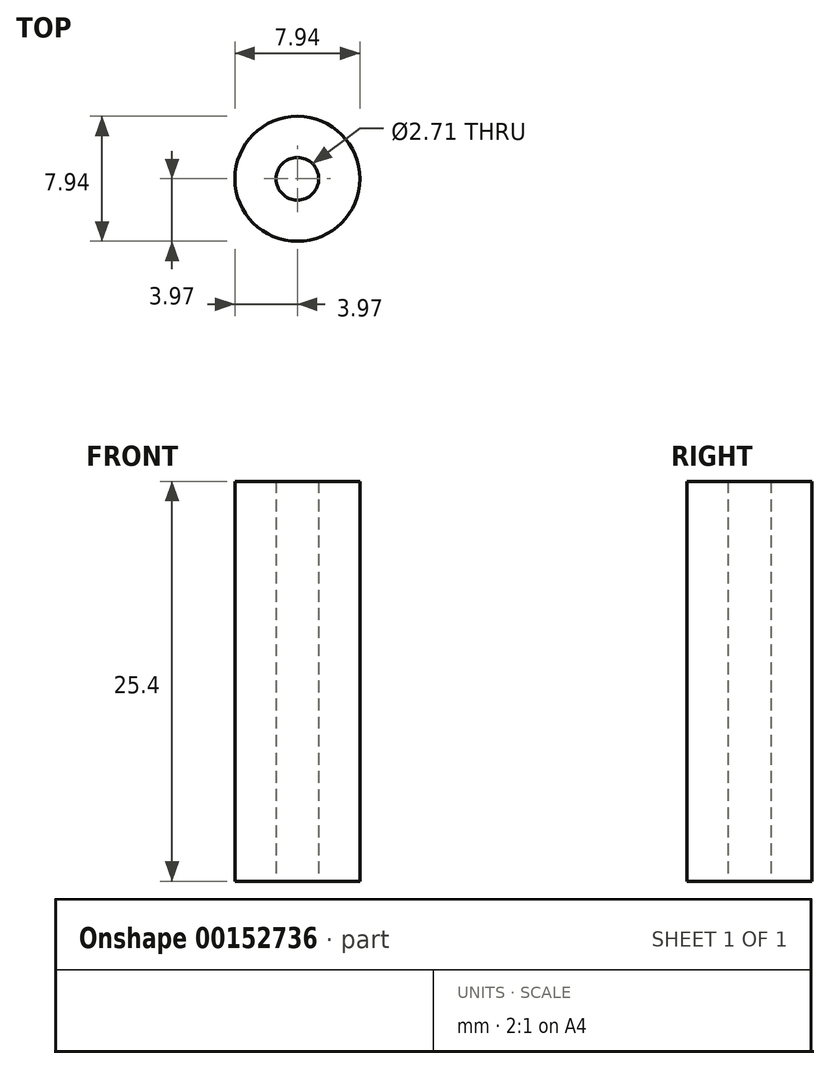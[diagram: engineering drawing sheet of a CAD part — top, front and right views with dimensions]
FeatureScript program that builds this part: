
annotation { "Feature Type Name" : "Feature", "Feature Type Description" : "" }
export const myFeature = defineFeature(function(context is Context, id is Id, definition is map)
    precondition{}
    {
        {
            var Q0;
            Q0=qCreatedBy(makeId("Top.planeOp"),FACE);
            var sketch = newSketch(context, id + "F0", { "sketchPlane" : qUnion([Q0])});
            skCircle(sketch, "E0", {"center": v(0, 0) * mm, "radius": 3.97 * mm});
            skCircle(sketch, "E1", {"center": v(0, 0) * mm, "radius": 1.35 * mm});
            skSolve(sketch);
        }
        {
            var Q0;
            Q0 = qSketchRegion(id + "F0", true);
            extrude(context, id + "F1", {"entities" : qUnion([Q0]), "depth" : 25.4 * mm});
        }
    });
